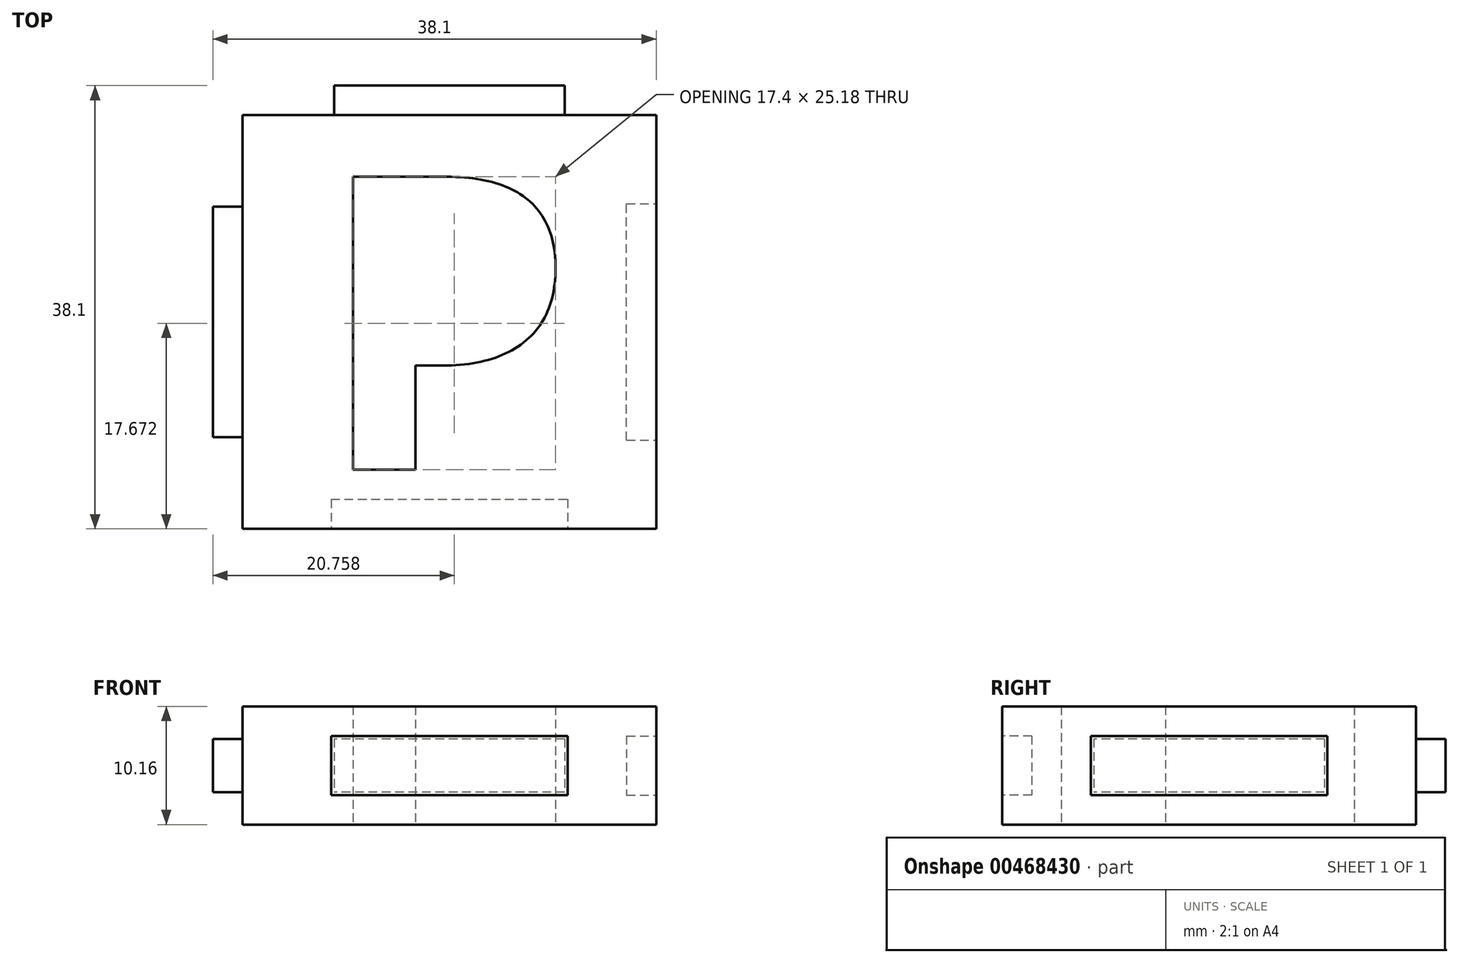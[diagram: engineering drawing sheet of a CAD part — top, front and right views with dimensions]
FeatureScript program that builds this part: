
annotation { "Feature Type Name" : "Feature", "Feature Type Description" : "" }
export const myFeature = defineFeature(function(context is Context, id is Id, definition is map)
    precondition{}
    {
        {
            var Q0;
            Q0=qCreatedBy(makeId("Top.planeOp"),FACE);
            var sketch = newSketch(context, id + "F0", { "sketchPlane" : qUnion([Q0])});
            skLineSegment(sketch, "E0.bottom", {"start": v(-17.78, 17.78) * mm, "end": v(17.78, 17.78) * mm});
            skLineSegment(sketch, "E0.top", {"start": v(-17.78, -17.78) * mm, "end": v(17.78, -17.78) * mm});
            skLineSegment(sketch, "E0.left", {"start": v(-17.78, 17.78) * mm, "end": v(-17.78, -17.78) * mm});
            skLineSegment(sketch, "E0.right", {"start": v(17.78, 17.78) * mm, "end": v(17.78, -17.78) * mm});
            skText(sketch, "E1", { "text": "P", "fontName": "OpenSans-Bold.ttf"});
            const initialGuessF0  = {"E1": [-0.01143, -0.0127, 1, 0, 0.0254]};
            skSetInitialGuess(sketch, initialGuessF0);
            skSolve(sketch);
        }
        {
            var Q0;
            Q0=qSketchRegion(id+"F0",true);
            extrude(context, id + "F1", {"entities" : qUnion([Q0]), "endBound" : BoundingType.SYMMETRIC, "depth" : 10.16 * mm});
        }
        {
            var Q0;
            Q0=makeQuery(id+"F1.opExtrude","SWEPT_FACE",FACE,{"disambiguationData":[OSD([sQuery(id+"F0.wireOp",EDGE,"E0.bottom")])]});
            var sketch = newSketch(context, id + "F2", { "sketchPlane" : qUnion([Q0])});
            skLineSegment(sketch, "E2.bottom", {"start": v(-9.9, 2.29) * mm, "end": v(9.9, 2.29) * mm});
            skLineSegment(sketch, "E2.top", {"start": v(-9.9, -2.29) * mm, "end": v(9.9, -2.29) * mm});
            skLineSegment(sketch, "E2.left", {"start": v(-9.9, 2.29) * mm, "end": v(-9.9, -2.29) * mm});
            skLineSegment(sketch, "E2.right", {"start": v(9.9, 2.29) * mm, "end": v(9.9, -2.29) * mm});
            skSolve(sketch);
        }
        {
            var Q0;
            Q0=qSketchRegion(id+"F2",true);
            extrude(context, id + "F3", {"entities" : qUnion([Q0]), "operationType" : NewBodyOperationType.ADD, "depth" : 2.54 * mm});
        }
        {
            var Q0;
            Q0=makeQuery(id+"F1.opExtrude","SWEPT_FACE",FACE,{"disambiguationData":[OSD([sQuery(id+"F0.wireOp",EDGE,"E0.left")])]});
            var sketch = newSketch(context, id + "F4", { "sketchPlane" : qUnion([Q0])});
            skLineSegment(sketch, "E3.bottom", {"start": v(-9.9, 2.29) * mm, "end": v(9.9, 2.29) * mm});
            skLineSegment(sketch, "E3.top", {"start": v(-9.9, -2.29) * mm, "end": v(9.9, -2.29) * mm});
            skLineSegment(sketch, "E3.left", {"start": v(-9.9, 2.29) * mm, "end": v(-9.9, -2.29) * mm});
            skLineSegment(sketch, "E3.right", {"start": v(9.9, 2.29) * mm, "end": v(9.9, -2.29) * mm});
            skSolve(sketch);
        }
        {
            var Q0;
            Q0=qSketchRegion(id+"F4",true);
            extrude(context, id + "F5", {"entities" : qUnion([Q0]), "operationType" : NewBodyOperationType.ADD, "depth" : 2.54 * mm});
        }
        {
            var Q0;
            Q0=makeQuery(id+"F1.opExtrude","SWEPT_FACE",FACE,{"disambiguationData":[OSD([sQuery(id+"F0.wireOp",EDGE,"E0.top")])]});
            var sketch = newSketch(context, id + "F6", { "sketchPlane" : qUnion([Q0])});
            skLineSegment(sketch, "E4.bottom", {"start": v(-10.16, 2.54) * mm, "end": v(10.16, 2.54) * mm});
            skLineSegment(sketch, "E4.top", {"start": v(-10.16, -2.54) * mm, "end": v(10.16, -2.54) * mm});
            skLineSegment(sketch, "E4.left", {"start": v(-10.16, 2.54) * mm, "end": v(-10.16, -2.54) * mm});
            skLineSegment(sketch, "E4.right", {"start": v(10.16, 2.54) * mm, "end": v(10.16, -2.54) * mm});
            skSolve(sketch);
        }
        {
            var Q0;
            Q0=qSketchRegion(id+"F6",true);
            extrude(context, id + "F7", {"entities" : qUnion([Q0]), "operationType" : NewBodyOperationType.REMOVE, "oppositeDirection" : true, "depth" : 2.54 * mm});
        }
        {
            var Q0;
            Q0=makeQuery(id+"F1.opExtrude","SWEPT_FACE",FACE,{"disambiguationData":[OSD([sQuery(id+"F0.wireOp",EDGE,"E0.right")])]});
            var sketch = newSketch(context, id + "F8", { "sketchPlane" : qUnion([Q0])});
            skLineSegment(sketch, "E5.bottom", {"start": v(-10.16, 2.54) * mm, "end": v(10.16, 2.54) * mm});
            skLineSegment(sketch, "E5.top", {"start": v(-10.16, -2.54) * mm, "end": v(10.16, -2.54) * mm});
            skLineSegment(sketch, "E5.left", {"start": v(-10.16, 2.54) * mm, "end": v(-10.16, -2.54) * mm});
            skLineSegment(sketch, "E5.right", {"start": v(10.16, 2.54) * mm, "end": v(10.16, -2.54) * mm});
            skSolve(sketch);
        }
        {
            var Q0;
            Q0=qSketchRegion(id+"F8",true);
            extrude(context, id + "F9", {"entities" : qUnion([Q0]), "operationType" : NewBodyOperationType.REMOVE, "oppositeDirection" : true, "depth" : 2.54 * mm});
        }
    });
